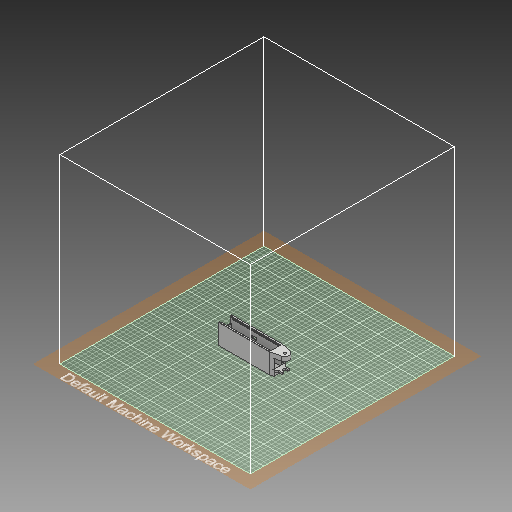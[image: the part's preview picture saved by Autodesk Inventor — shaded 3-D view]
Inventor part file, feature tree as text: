
AUTODESK INVENTOR PART (.ipt)
format: ipt  version: 2019 (Build 230136000, 136)  size: 680,960 bytes
history: native  units: mm
features: sketch x18, extrude x16, plane x2, chamfer x2, sweep x1, shell x1, hole x1, mirror x1, projected_geometry x1
ambient origin geometry x8: Origin, YZ Plane, XZ Plane, XY Plane, X Axis, Y Axis, Z Axis, Center Point
bodies: Body1 (feature_tree)
feature tree (43):
  sweep  "Sweep1"
  shell  "Shell1"  Thickness=15.0mm
  hole  "Hole4"  [1 undecoded]
  extrude  "Extrusion4"  Depth=25.0mm
  extrude  "Extrusion5"  Depth=88.0mm
  plane  "Work Plane4"
  extrude  "Extrusion6"  Depth=8.0mm
  extrude  "Extrusion7"  Depth=10.0mm TaperAngle=0.0deg
  extrude  "Extrusion12"  Depth=22.7mm
  extrude  "Extrusion11"  Depth=10.0mm TaperAngle=0.0deg
  extrude  "Extrusion10"  Depth=4.0mm TaperAngle=0.0deg
  plane  "Work Plane5"
  extrude  "Extrusion15"  Depth=8.0mm
  mirror  "Mirror1"
  extrude  "Extrusion16"  Depth=4.0mm TaperAngle=0.0deg
  extrude  "Extrusion19"  Depth=12.0mm
  extrude  "Extrusion24"  Depth=1.5mm
  extrude  "Extrusion25"  Depth=1.5mm
  extrude  "Extrusion26"  Depth=1.5mm
  extrude  "Extrusion27"  Depth=15.0mm
  chamfer  "Chamfer1"  Distance=1.5mm
  chamfer  "Chamfer2"  Distance=3.0mm
  extrude  "Extrusion28"  Depth=3.0mm
  extrude  "Extrusion29"  Depth=1.5mm TaperAngle=0.0deg
  sketch  "Sketch5"  dims[d25=42.0mm d28=0.0mm d29=0.0mm d52=15.0mm]
  sketch  "Sketch6"  dims[d53=20.0mm d54=5.5mm]
  sketch  "Sketch12"  dims[d55=110.0mm d56=25.0mm]
  sketch  "Sketch14"  dims[d57=2.0mm d58=88.0mm]
  sketch  "Sketch15"  dims[d59=10.0mm]
  sketch  "Sketch16"  dims[d60=5.5mm d61=6.0mm d62=15.0mm d63=4.3mm d64=90.0deg d65=8.0mm d66=20.594885mm d67=5.5mm]
  sketch  "Sketch17"  dims[d68=19.0mm d69=10.0mm d70=0.0mm]
  sketch  "Sketch20"  dims[d71=10.0mm d72=0.0mm d73=22.7mm]
  sketch  "Sketch21"  dims[d74=25.0mm d75=10.0mm d76=0.0mm]
  sketch  "Sketch22"  dims[d77=8.0mm d78=4.0mm d79=0.0mm]
  sketch  "Sketch25"  dims[d90=2.0mm d91=0.0mm d92=8.0mm]
  projected_geometry  "Projected Loop1"
  sketch  "Sketch29"  dims[d93=8.0mm d94=4.0mm d95=0.0mm]
  sketch  "Sketch36"  dims[d96=12.0mm d97=12.0mm]
  sketch  "Sketch37"  dims[d98=4.0mm d99=0.0mm d105=1.5mm]
  sketch  "Sketch38"  dims[d106=1.5mm d107=1.5mm]
  sketch  "Sketch39"  dims[d108=1.5mm d109=0.0mm d110=1.5mm]
  sketch  "Sketch40"  dims[d111=1.5mm d112=15.0mm d113=1.5mm d114=0.0mm]
  sketch  "Sketch41"  dims[d123=3.0mm d125=3.0mm d127=3.0mm d128=1.5mm d129=0.0mm d132=45.0deg d133=45.0deg d134=2.0mm d136=7.0mm d138=0.75mm d139=0.75mm d149=10.0mm d150=0.0mm d151=2.0mm d152=10.0mm d153=0.0mm d154=15.0mm d155=13.0mm d156=0.0mm d157=4.0mm d158=8.0mm d159=15.0mm d160=0.0mm d161=5.0mm d162=2.0mm d163=45.0deg d164=2.0mm d165=2.0mm d166=45.0deg d167=8.55mm d168=0.1mm d169=0.0mm d172=10.0mm d173=0.0mm d176=51.0mm d177=5.0mm d179=17.65mm d38=1.0mm d39=1.0mm d40=8.0mm d41=0.15mm d42=3.4mm d43=0.375mm d44=14.3117mm d45=0.75mm d46=20.594885mm d47=0.0625mm d48=0.75mm d49=0.375mm]
note: 1 required parameter value undecoded (feature->parameter linkage not recoverable at this tier; creation-order binding heuristic only, values carry confidence <= 0.55)
